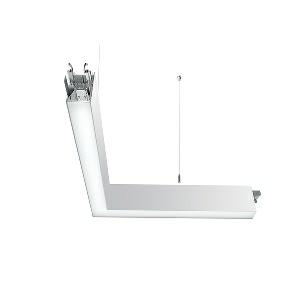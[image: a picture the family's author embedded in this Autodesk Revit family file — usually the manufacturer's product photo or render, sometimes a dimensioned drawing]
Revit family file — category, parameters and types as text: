
# Revit family: idoo_line_-_ilp_3000_vtl_d_lr_mid_00807709_3c10
name_source: partatom
category: Lighting Fixtures
units: mm (PartAtom-declared; Revit-internal decimal feet)

## family parameters
Cut with Voids When Loaded = No
Host = Face
Light Source = No
Part Type = Normal
Room Calculation Point = No
Round Connector Dimension = Use Diameter
Shared = No

## types (1)
- IDOO.line - ILP 3000/VTL/D/LR MID (1 x LED, 3150 lm, 2700-6500K)
    Apparent Load = 32 VA
    Approval mark = CE
    CIE Flux Codes = 66 91 98 40 100
    Color Rendering = 90-100
    Color Temperature = 2700-6500K
    Control Gear = Electronic ballast
    Default Elevation = 1800 mm
    Description = ILP 3000/VTL/D|Suspended luminaire|light source: LED|connected load: 220-240 V, 50/60 Hz|Power consumption: approx. 32 W|standby: approx. 0,25|luminous flux: 3150 lm|luminous efficacy: 98 lm/W|light distribution: Direct/indirect|direct ratio: approx. 40 %|colour temperature: Cold white, ca. 2700-6500 K|color rendering index (CRI): >= 90|chromaticity tolerance:  3 SDCM|System of protection: IP 40|technology: Continuously dimmable|luminaire body|material: Sectional aluminium|colour: White|lamp cover: Acrylic (PMMA), Clear|Fastening: Steel cable 0.3 - 0.7 m|glare control: Prism aperture|luminance(L65): <= 2700 cd/m|unified glare rating(4H 8H): <=  16|special features: Specified values at approx. 4000 K, DALI Load 1x, Through-wired, up to 18 m on one mains connection, External control required for Dali Device type 8, Flicker-free, Constant luminous flux between 2700 and 6500 K, Constant colour temperature over the whole dimming range, Continous light without dark z, Suitable as emergency lighting, 90░ rerouting on the right sid, Mechanical and electrical connection of the individual modules without tools|
    Frequency = 50 Hz
    Height = 110 mm
    Lamp = 1 x LED
    Lamp Light Flux = 3150 lm
    Lamp count = 1
    Length = 600 mm
    Luminous efficacy = 98 lm/W
    Manufacturer = Waldmann
    ModVariant = No
    Model = 00807709
    Mounting Place = Ceiling
    Mounting Type = Pendant
    Number of Poles = 1
    OnlyDefault = Yes
    Power Factor = 1
    Product Name = IDOO.line - ILP 3000/VTL/D/LR MID
    Product group = Suspended luminaire
    ProductGroupID = 9
    Protection Class = Protection class I
    Protection Degree = IP 40
    RLX_Detail_Level = 1
    RLX_Emergency_Light_Flux = 0 lm
    RLX_Emergency_Type = 0
    RLX_Emergency_Type_DB = No
    RlxData = <blob elided: 21373 chars, md5=a1833574>
    Socket = socket
    Standby Power = 0 W
    System Light Flux = 3150 lm
    System Power = 32 W
    Type Comments = Product without accessories
    Type Image = ilp_dlp_lr_ws.jpg
    URL = http://relux.com
    VarID = ---
    Voltage = 230 V
    Voltage Range = 220-240 V
    Weight = 0.00 kg
    Width = 600 mm

## geometry (parser evidence)
native form markers: Blend x4, Sweep x13
no freeform markers — native parametric forms only
